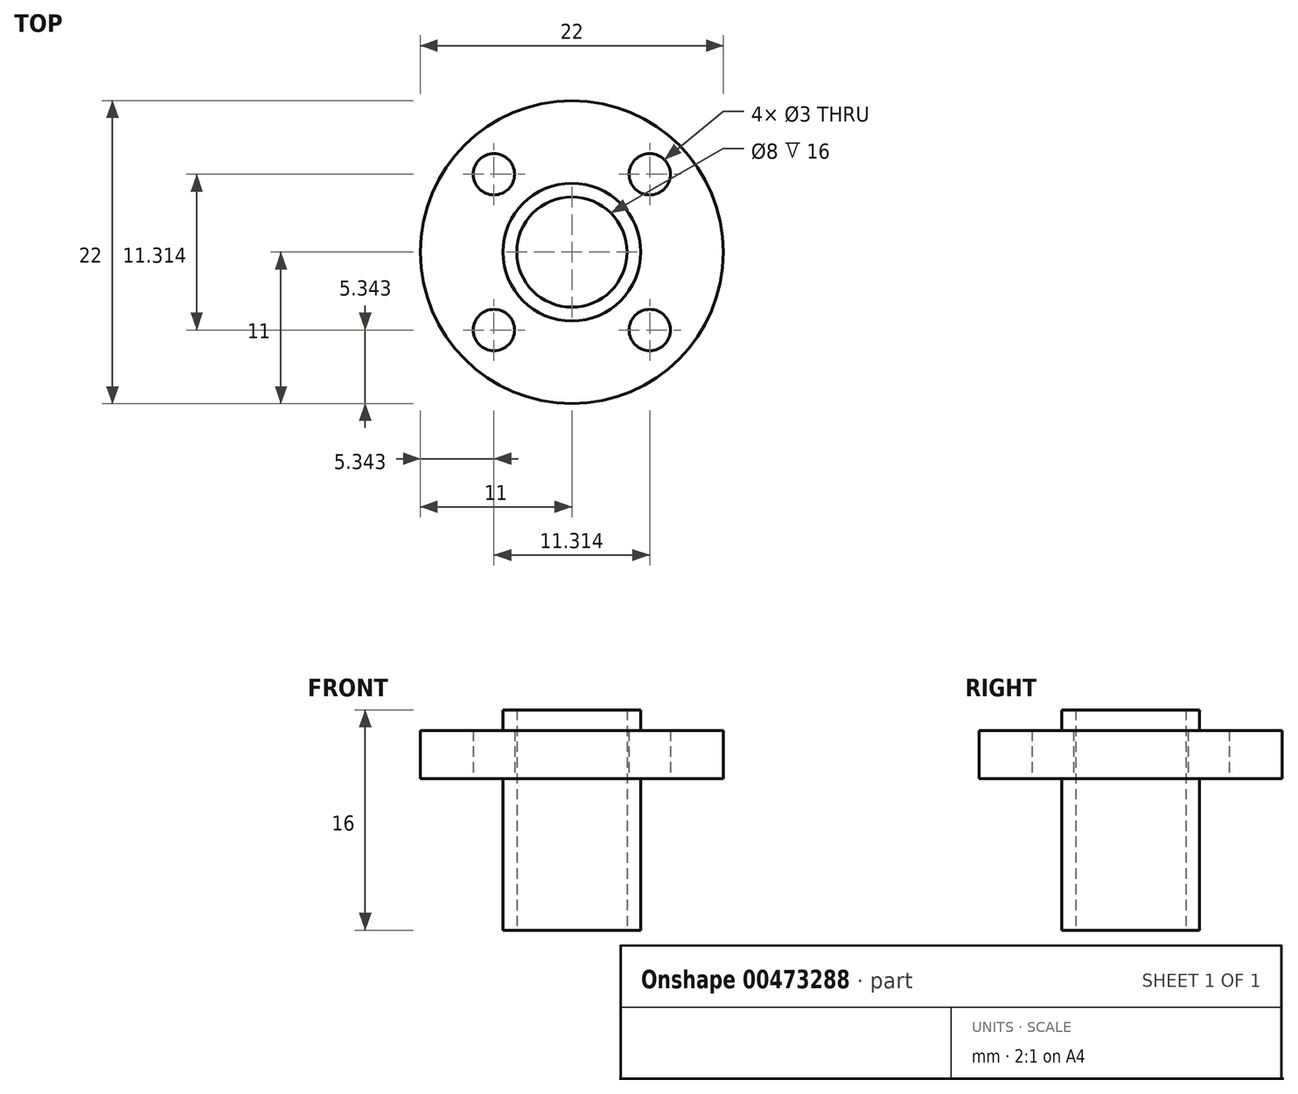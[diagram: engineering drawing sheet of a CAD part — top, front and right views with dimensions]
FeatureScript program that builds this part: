
annotation { "Feature Type Name" : "Feature", "Feature Type Description" : "" }
export const myFeature = defineFeature(function(context is Context, id is Id, definition is map)
    precondition{}
    {
        {
            var Q0;
            Q0=qCreatedBy(makeId("Top.planeOp"),FACE);
            var sketch = newSketch(context, id + "F0", { "sketchPlane" : qUnion([Q0])});
            skCircle(sketch, "E0", {"center": v(0, 0) * mm, "radius": 4 * mm});
            skCircle(sketch, "E1", {"center": v(-5.66, 5.66) * mm, "radius": 1.5 * mm});
            skCircle(sketch, "E2.MirrorC", {"center": v(5.66, 5.66) * mm, "radius": 1.5 * mm});
            skCircle(sketch, "E3.MirrorC", {"center": v(-5.66, -5.66) * mm, "radius": 1.5 * mm});
            skCircle(sketch, "E4.MirrorC", {"center": v(5.66, -5.66) * mm, "radius": 1.5 * mm});
            skCircle(sketch, "E5", {"center": v(0, 0) * mm, "radius": 11 * mm});
            skSolve(sketch);
        }
        {
            var Q0;
            Q0 = qSketchRegion(id + "F0", true);
            extrude(context, id + "F1", {"entities" : qUnion([Q0]), "depth" : 3.5 * mm, "offsetDistance" : 25 * mm});
        }
        {
            var Q0;
            Q0=makeQuery(id+"F1.opExtrude","CAP_FACE",FACE,{"disambiguationData":[OSD([sQuery(id+"F0.wireOp",EDGE,"E0"),sQuery(id+"F0.wireOp",EDGE,"E1"),sQuery(id+"F0.wireOp",EDGE,"E2.MirrorC"),sQuery(id+"F0.wireOp",EDGE,"E3.MirrorC"),sQuery(id+"F0.wireOp",EDGE,"E4.MirrorC"),sQuery(id+"F0.wireOp",EDGE,"E5")])],"isStart":true});
            var sketch = newSketch(context, id + "F2", { "sketchPlane" : qUnion([Q0])});
            skCircle(sketch, "E6.0", {"center": v(0, 0) * mm, "radius": 4 * mm});
            skCircle(sketch, "E7", {"center": v(0, 0) * mm, "radius": 5 * mm});
            skSolve(sketch);
        }
        {
            var Q0;
            Q0 = qSketchRegion(id + "F2", true);
            extrude(context, id + "F3", {"entities" : qUnion([Q0]), "operationType" : NewBodyOperationType.ADD, "depth" : 11 * mm, "offsetDistance" : 25 * mm, "hasSecondDirection" : true, "secondDirectionOppositeDirection" : true, "secondDirectionDepth" : 5 * mm});
        }
    });
